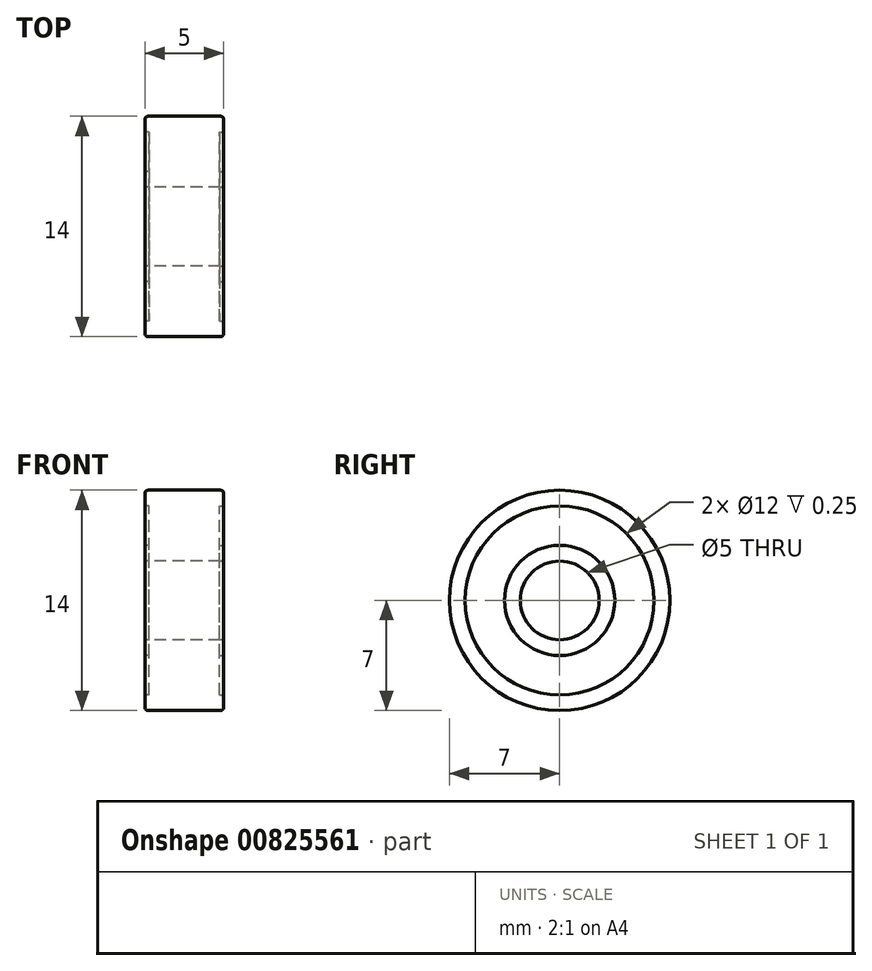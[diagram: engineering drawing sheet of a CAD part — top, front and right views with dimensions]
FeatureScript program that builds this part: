
annotation { "Feature Type Name" : "Feature", "Feature Type Description" : "" }
export const myFeature = defineFeature(function(context is Context, id is Id, definition is map)
    precondition{}
    {
        {
            var Q0;
            Q0=qCreatedBy(makeId("Right.planeOp"),FACE);
            var sketch = newSketch(context, id + "F0", { "sketchPlane" : qUnion([Q0])});
            skCircle(sketch, "E0", {"center": v(0, 0) * mm, "radius": 7 * mm});
            skCircle(sketch, "E1", {"center": v(0, 0) * mm, "radius": 2.5 * mm});
            skSolve(sketch);
        }
        {
            var Q0;
            Q0=qSketchRegion(id+"F0",true);
            extrude(context, id + "F1", {"entities" : qUnion([Q0]), "depth" : 5 * mm});
        }
        {
            var Q0;
            Q0=qCreatedBy(makeId("Right.planeOp"),FACE);
            var sketch = newSketch(context, id + "F2", { "sketchPlane" : qUnion([Q0])});
            skCircle(sketch, "E2", {"center": v(0, 0) * mm, "radius": 6 * mm});
            skCircle(sketch, "E3", {"center": v(0, 0) * mm, "radius": 3.5 * mm});
            skSolve(sketch);
        }
        {
            var Q0;
            Q0=qSketchRegion(id+"F2",true);
            extrude(context, id + "F3", {"entities" : qUnion([Q0]), "operationType" : NewBodyOperationType.REMOVE, "depth" : 0.25 * mm});
        }
        {
            var Q0;
            Q0=makeQuery(id+"F1.opExtrude","CAP_FACE",FACE,{"disambiguationData":[OSD([sQuery(id+"F0.wireOp",EDGE,"E0"),sQuery(id+"F0.wireOp",EDGE,"E1")])],"isStart":false});
            var sketch = newSketch(context, id + "F4", { "sketchPlane" : qUnion([Q0])});
            skCircle(sketch, "E4", {"center": v(0, 0) * mm, "radius": 6 * mm});
            skCircle(sketch, "E5", {"center": v(0, 0) * mm, "radius": 3.5 * mm});
            skSolve(sketch);
        }
        {
            var Q0;
            Q0=qSketchRegion(id+"F4",true);
            extrude(context, id + "F5", {"entities" : qUnion([Q0]), "operationType" : NewBodyOperationType.REMOVE, "oppositeDirection" : true, "depth" : 0.25 * mm});
        }
        {
            var Q0;
            Q0=makeQuery(id+"F1.opExtrude","SWEPT_FACE",FACE,{"disambiguationData":[OSD([sQuery(id+"F0.wireOp",EDGE,"E0")])]});
            var Q1;
            Q1=makeQuery(id+"F1.opExtrude","SWEPT_FACE",FACE,{"disambiguationData":[OSD([sQuery(id+"F0.wireOp",EDGE,"E1")])]});
            fillet(context, id + "F6", {"entities" : qUnion([Q0, Q1]), "radius" : 0.2 * mm, "tangentPropagation" : true, "allowEdgeOverflow" : false});
        }
    });
